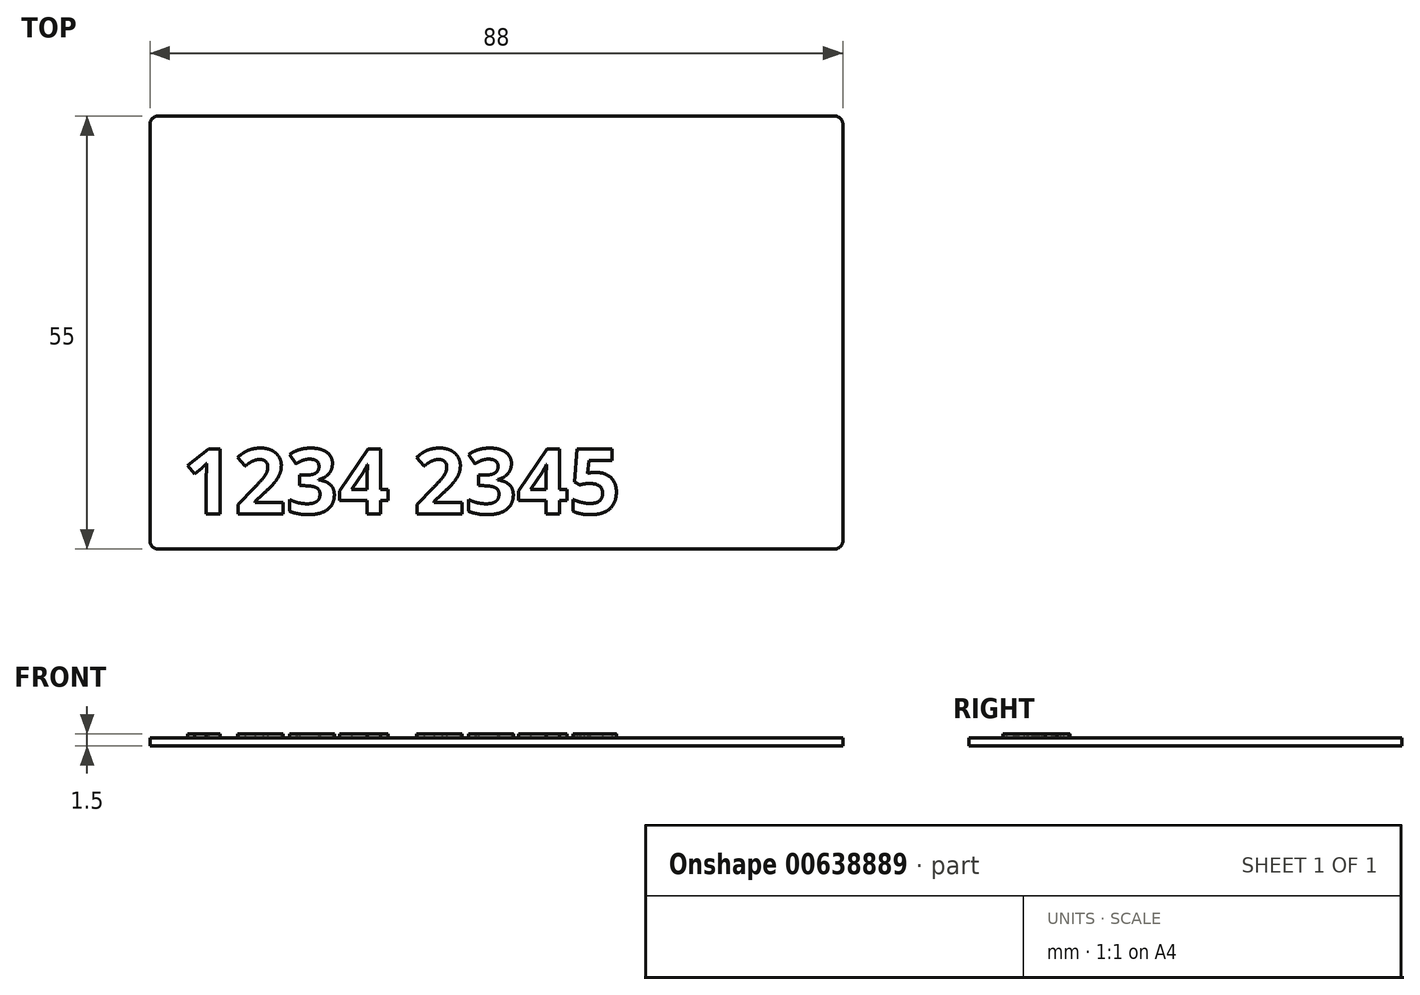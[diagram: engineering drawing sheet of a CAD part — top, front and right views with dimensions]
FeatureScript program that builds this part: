
annotation { "Feature Type Name" : "Feature", "Feature Type Description" : "" }
export const myFeature = defineFeature(function(context is Context, id is Id, definition is map)
    precondition{}
    {
        {
            var Q0;
            Q0=qCreatedBy(makeId("Top.planeOp"),FACE);
            var sketch = newSketch(context, id + "F0", { "sketchPlane" : qUnion([Q0])});
            skLineSegment(sketch, "E0.bottom", {"start": v(43, -27.5) * mm, "end": v(-43, -27.5) * mm});
            skLineSegment(sketch, "E0.top", {"start": v(43, 27.5) * mm, "end": v(-43, 27.5) * mm});
            skLineSegment(sketch, "E0.left", {"start": v(44, -26.5) * mm, "end": v(44, 26.5) * mm});
            skLineSegment(sketch, "E0.right", {"start": v(-44, -26.5) * mm, "end": v(-44, 26.5) * mm});
            skPoint(sketch, "E0.middle", {"position": v(0, 0) * mm});
            skPoint(sketch, "E1.visualSharp", {"position": v(-44, 27.5) * mm});
            skArc(sketch, "E1.filletArc", {"start": v(-43, 27.5) * mm, "mid": v(-43.7, 27.2) * mm, "end": v(-44, 26.5) * mm});
            skPoint(sketch, "E2.visualSharp", {"position": v(-44, -27.5) * mm});
            skArc(sketch, "E2.filletArc", {"start": v(-44, -26.5) * mm, "mid": v(-43.7, -27.2) * mm, "end": v(-43, -27.5) * mm});
            skPoint(sketch, "E3.visualSharp", {"position": v(44, -27.5) * mm});
            skArc(sketch, "E3.filletArc", {"start": v(43, -27.5) * mm, "mid": v(43.7, -27.2) * mm, "end": v(44, -26.5) * mm});
            skPoint(sketch, "E4.visualSharp", {"position": v(44, 27.5) * mm});
            skArc(sketch, "E4.filletArc", {"start": v(44, 26.5) * mm, "mid": v(43.7, 27.2) * mm, "end": v(43, 27.5) * mm});
            skSolve(sketch);
        }
        {
            var Q0;
            Q0=makeQuery(id+"F0.imprint","IMPRINT",FACE,{"disambiguationData":[TD([[makeQuery(id+"F0.imprint","IMPRINT",EDGE,{"derivedFrom":sQuery(id+"F0.wireOp",EDGE,"E0.bottom")}),-1.0]])]});
            extrude(context, id + "F1", {"entities" : qUnion([Q0]), "depth" : 1 * mm, "offsetDistance" : 25 * mm});
        }
        {
            var Q0;
            Q0=makeQuery(id+"F1.opExtrude","CAP_FACE",FACE,{"disambiguationData":[OSD([sQuery(id+"F0.wireOp",EDGE,"E0.bottom"),sQuery(id+"F0.wireOp",EDGE,"E0.top"),sQuery(id+"F0.wireOp",EDGE,"E0.left"),sQuery(id+"F0.wireOp",EDGE,"E0.right"),sQuery(id+"F0.wireOp",EDGE,"E1.filletArc"),sQuery(id+"F0.wireOp",EDGE,"E2.filletArc"),sQuery(id+"F0.wireOp",EDGE,"E3.filletArc"),sQuery(id+"F0.wireOp",EDGE,"E4.filletArc")])],"isStart":false});
            var sketch = newSketch(context, id + "F2", { "sketchPlane" : qUnion([Q0])});
            skText(sketch, "E5", { "text": "1234 2345", "fontName": "OpenSans-Bold.ttf"});
            const initialGuessF2  = {"E5": [-0.03988, -0.02302, 1, 0, 0.0083]};
            skSetInitialGuess(sketch, initialGuessF2);
            skSolve(sketch);
        }
        {
            var Q0;
            Q0 = qSketchRegion(id + "F2", true);
            extrude(context, id + "F3", {"entities" : qUnion([Q0]), "operationType" : NewBodyOperationType.ADD, "depth" : 0.5 * mm, "offsetDistance" : 25 * mm});
        }
    });
